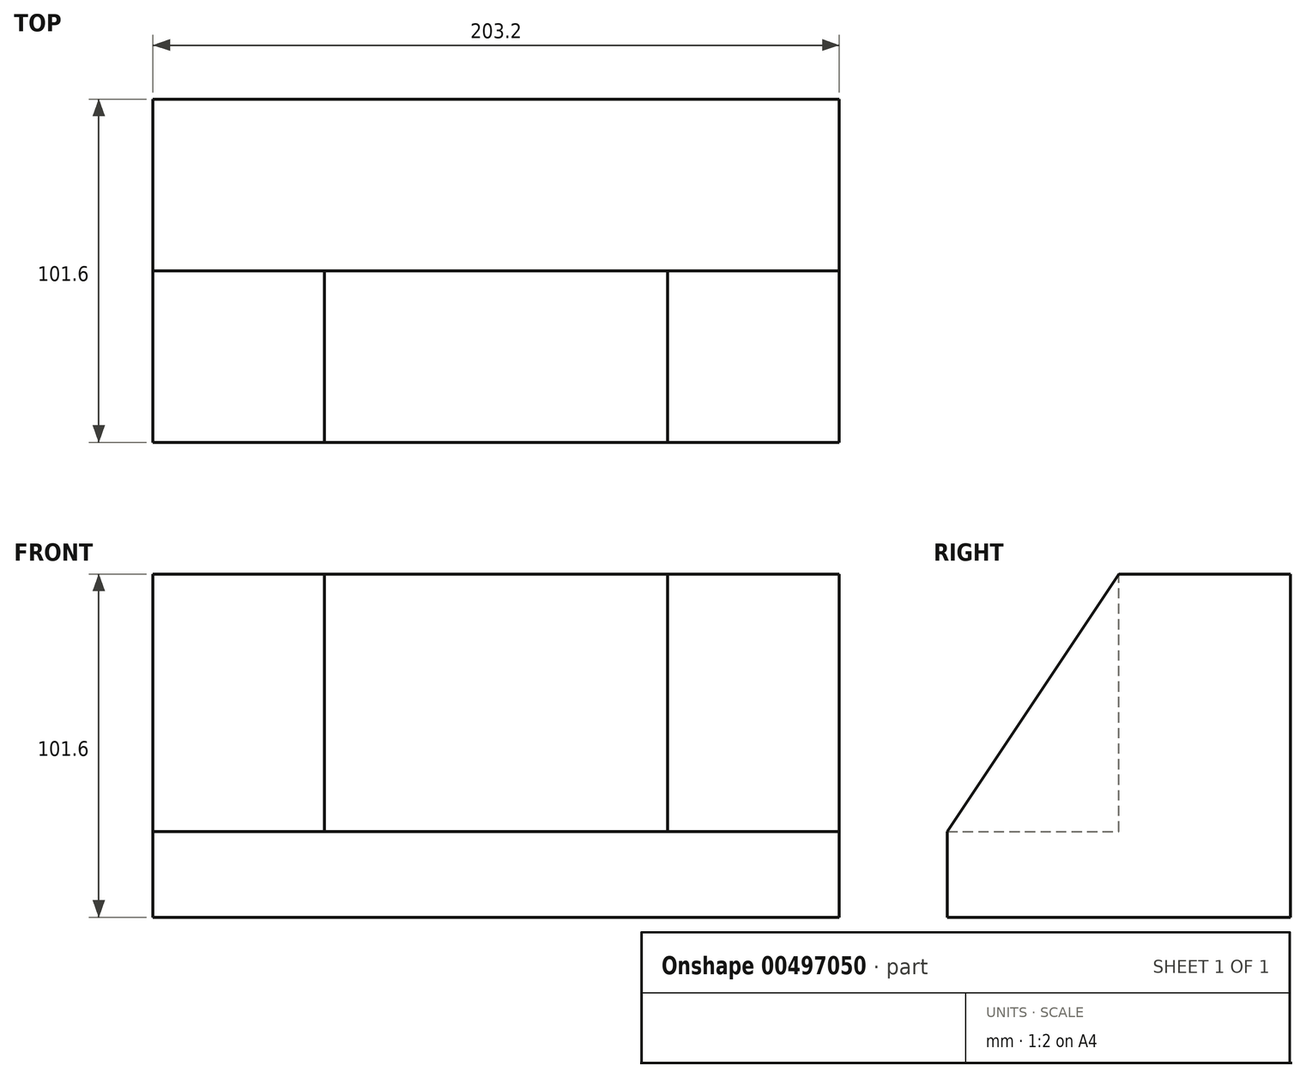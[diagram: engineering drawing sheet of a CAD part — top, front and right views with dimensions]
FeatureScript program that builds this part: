
annotation { "Feature Type Name" : "Feature", "Feature Type Description" : "" }
export const myFeature = defineFeature(function(context is Context, id is Id, definition is map)
    precondition{}
    {
        {
            var Q0;
            Q0=qCreatedBy(makeId("Front.planeOp"),FACE);
            var sketch = newSketch(context, id + "F0", { "sketchPlane" : qUnion([Q0])});
            skLineSegment(sketch, "E0", {"start": v(-71.77, -62.2) * mm, "end": v(131.43, -62.2) * mm});
            skLineSegment(sketch, "E1", {"start": v(131.43, -62.2) * mm, "end": v(131.43, -36.8) * mm});
            skLineSegment(sketch, "E2", {"start": v(131.43, -36.8) * mm, "end": v(-71.77, -36.8) * mm});
            skLineSegment(sketch, "E3", {"start": v(-71.77, -36.8) * mm, "end": v(-71.77, -62.2) * mm});
            skSolve(sketch);
        }
        {
            var Q0;
            Q0=makeQuery(id+"F0.imprint","IMPRINT",FACE,{"disambiguationData":[TD([[makeQuery(id+"F0.imprint","IMPRINT",EDGE,{"derivedFrom":sQuery(id+"F0.wireOp",EDGE,"E0")}),1.0]])]});
            extrude(context, id + "F1", {"entities" : qUnion([Q0]), "depth" : 101.6 * mm});
        }
        {
            var Q0;
            Q0=makeQuery(id+"F1.opExtrude","SWEPT_FACE",FACE,{"disambiguationData":[OSD([sQuery(id+"F0.wireOp",EDGE,"E1")])]});
            var sketch = newSketch(context, id + "F2", { "sketchPlane" : qUnion([Q0])});
            skLineSegment(sketch, "E4", {"start": v(0, -36.8) * mm, "end": v(0, 39.4) * mm});
            skLineSegment(sketch, "E5", {"start": v(0, 39.4) * mm, "end": v(-50.8, 39.4) * mm});
            skLineSegment(sketch, "E6", {"start": v(-50.8, 39.4) * mm, "end": v(-101.6, -36.8) * mm});
            skSolve(sketch);
        }
        {
            var Q0;
            Q0=makeQuery(id+"F2.imprint","IMPRINT",FACE,{"disambiguationData":[TD([[makeQuery(id+"F2.imprint","IMPRINT",EDGE,{"derivedFrom":sQuery(id+"F2.wireOp",EDGE,"E4")}),1.0]])]});
            extrude(context, id + "F3", {"entities" : qUnion([Q0]), "operationType" : NewBodyOperationType.ADD, "depth" : -50.8 * mm});
        }
        {
            var Q0;
            Q0=makeQuery(id+"F1.opExtrude","SWEPT_FACE",FACE,{"disambiguationData":[OSD([sQuery(id+"F0.wireOp",EDGE,"E3")])]});
            var sketch = newSketch(context, id + "F4", { "sketchPlane" : qUnion([Q0])});
            skLineSegment(sketch, "E7", {"start": v(0, -36.8) * mm, "end": v(0, 39.4) * mm});
            skLineSegment(sketch, "E8", {"start": v(0, 39.4) * mm, "end": v(50.8, 39.4) * mm});
            skLineSegment(sketch, "E9", {"start": v(50.8, 39.4) * mm, "end": v(101.6, -36.8) * mm});
            skSolve(sketch);
        }
        {
            var Q0;
            Q0=makeQuery(id+"F4.imprint","IMPRINT",FACE,{"disambiguationData":[TD([[makeQuery(id+"F4.imprint","IMPRINT",EDGE,{"derivedFrom":sQuery(id+"F4.wireOp",EDGE,"E7")}),-1.0]])]});
            extrude(context, id + "F5", {"entities" : qUnion([Q0]), "operationType" : NewBodyOperationType.ADD, "depth" : -50.8 * mm});
        }
        {
            var Q0;
            Q0=makeQuery(id+"F5.opExtrude","SWEPT_FACE",FACE,{"disambiguationData":[OSD([sQuery(id+"F4.wireOp",EDGE,"E8")])]});
            var sketch = newSketch(context, id + "F6", { "sketchPlane" : qUnion([Q0])});
            skLineSegment(sketch, "E10", {"start": v(-20.97, 0) * mm, "end": v(80.63, 0) * mm});
            skLineSegment(sketch, "E11", {"start": v(80.63, 0) * mm, "end": v(80.63, -50.8) * mm});
            skLineSegment(sketch, "E12", {"start": v(80.63, -50.8) * mm, "end": v(-20.97, -50.8) * mm});
            skLineSegment(sketch, "E13", {"start": v(-20.97, -50.8) * mm, "end": v(-20.97, 0) * mm});
            skSolve(sketch);
        }
        {
            var Q0;
            Q0=makeQuery(id+"F6.imprint","IMPRINT",FACE,{"disambiguationData":[TD([[makeQuery(id+"F6.imprint","IMPRINT",EDGE,{"derivedFrom":sQuery(id+"F6.wireOp",EDGE,"E10")}),-1.0]])]});
            extrude(context, id + "F7", {"entities" : qUnion([Q0]), "operationType" : NewBodyOperationType.ADD, "depth" : -76.2 * mm});
        }
    });
